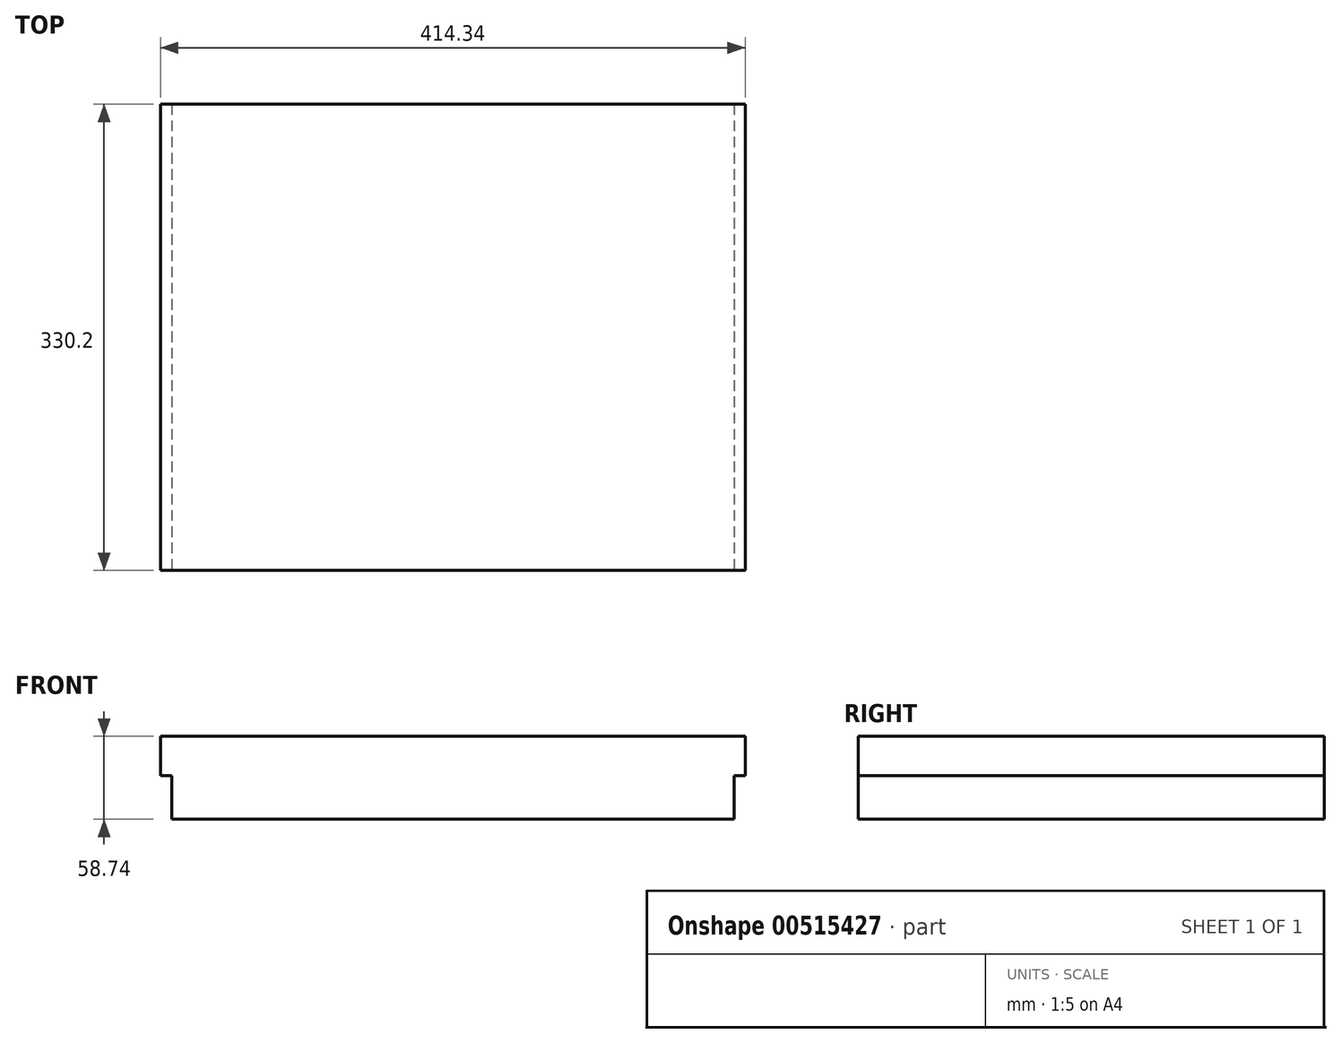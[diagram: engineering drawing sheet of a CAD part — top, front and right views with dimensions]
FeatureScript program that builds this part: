
annotation { "Feature Type Name" : "Feature", "Feature Type Description" : "" }
export const myFeature = defineFeature(function(context is Context, id is Id, definition is map)
    precondition{}
    {
        {
            var Q0;
            Q0=qCreatedBy(makeId("Front.planeOp"),FACE);
            var sketch = newSketch(context, id + "F0", { "sketchPlane" : qUnion([Q0])});
            skLineSegment(sketch, "E0.bottom", {"start": v(207.17, -29.37) * mm, "end": v(-207.17, -29.37) * mm, "construction": true});
            skLineSegment(sketch, "E0.top", {"start": v(207.17, 29.37) * mm, "end": v(-207.17, 29.37) * mm, "construction": true});
            skLineSegment(sketch, "E0.left", {"start": v(207.17, -29.37) * mm, "end": v(207.17, 29.37) * mm, "construction": true});
            skLineSegment(sketch, "E0.right", {"start": v(-207.17, -29.37) * mm, "end": v(-207.17, 29.37) * mm, "construction": true});
            skPoint(sketch, "E0.middle", {"position": v(0, 0) * mm});
            skLineSegment(sketch, "E1", {"start": v(0, 29.37) * mm, "end": v(0, -29.37) * mm, "construction": true});
            skLineSegment(sketch, "E2", {"start": v(0, 29.37) * mm, "end": v(-207.17, 29.37) * mm});
            skLineSegment(sketch, "E3", {"start": v(-207.17, 29.37) * mm, "end": v(-207.17, 1.43) * mm});
            skLineSegment(sketch, "E4", {"start": v(-207.17, 1.43) * mm, "end": v(-199.23, 1.43) * mm});
            skLineSegment(sketch, "E5", {"start": v(-199.23, 1.43) * mm, "end": v(-199.23, -29.37) * mm});
            skLineSegment(sketch, "E6", {"start": v(-199.23, -29.37) * mm, "end": v(0, -29.37) * mm});
            skLineSegment(sketch, "E7.MirrorCS", {"start": v(207.17, 1.43) * mm, "end": v(199.23, 1.43) * mm});
            skLineSegment(sketch, "E8.MirrorCS", {"start": v(199.23, -29.37) * mm, "end": v(0, -29.37) * mm});
            skLineSegment(sketch, "E9.MirrorCS", {"start": v(199.23, 1.43) * mm, "end": v(199.23, -29.37) * mm});
            skLineSegment(sketch, "E10.MirrorCS", {"start": v(207.17, 29.37) * mm, "end": v(207.17, 1.43) * mm});
            skLineSegment(sketch, "E11.MirrorCS", {"start": v(0, 29.37) * mm, "end": v(207.17, 29.37) * mm});
            skSolve(sketch);
        }
        {
            var Q0;
            Q0=makeQuery(id+"F0.imprint","IMPRINT",FACE,{"disambiguationData":[TD([[makeQuery(id+"F0.imprint","IMPRINT",EDGE,{"derivedFrom":sQuery(id+"F0.wireOp",EDGE,"E2")}),1.0]])]});
            extrude(context, id + "F1", {"entities" : qUnion([Q0]), "oppositeDirection" : true, "depth" : 330.2 * mm, "offsetDistance" : 25.4 * mm});
        }
    });
